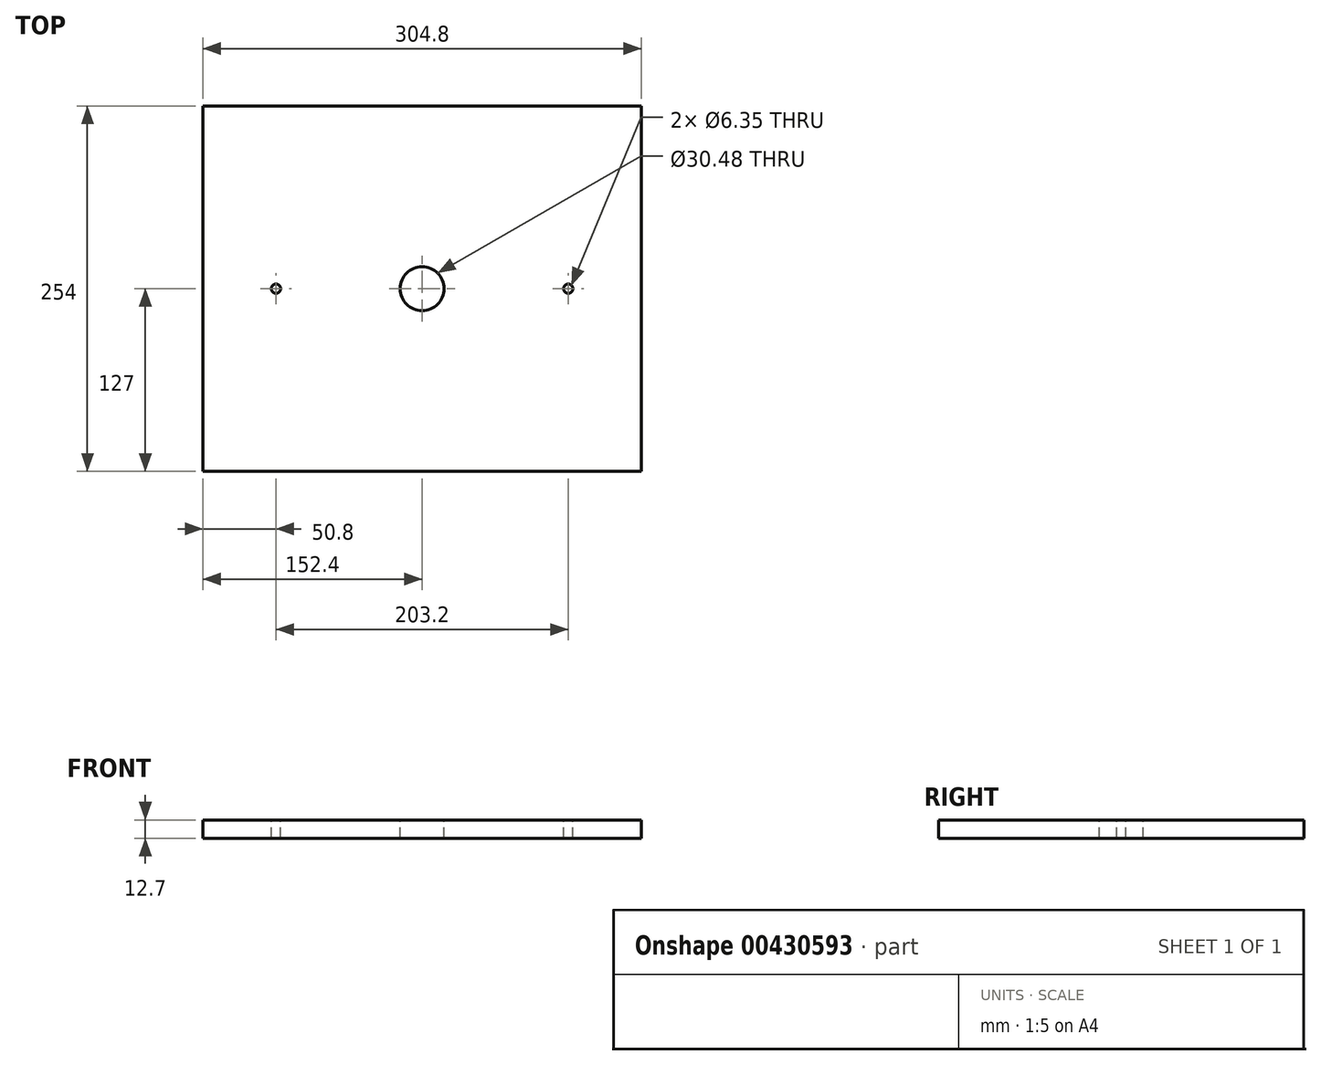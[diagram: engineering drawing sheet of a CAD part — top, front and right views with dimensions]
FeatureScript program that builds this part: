
annotation { "Feature Type Name" : "Feature", "Feature Type Description" : "" }
export const myFeature = defineFeature(function(context is Context, id is Id, definition is map)
    precondition{}
    {
        {
            var Q0;
            Q0=qCreatedBy(makeId("Top.planeOp"),FACE);
            var sketch = newSketch(context, id + "F0", { "sketchPlane" : qUnion([Q0])});
            skLineSegment(sketch, "E0.bottom", {"start": v(152.4, -127) * mm, "end": v(-152.4, -127) * mm});
            skLineSegment(sketch, "E0.top", {"start": v(152.4, 127) * mm, "end": v(-152.4, 127) * mm});
            skLineSegment(sketch, "E0.left", {"start": v(152.4, -127) * mm, "end": v(152.4, 127) * mm});
            skLineSegment(sketch, "E0.right", {"start": v(-152.4, -127) * mm, "end": v(-152.4, 127) * mm});
            skPoint(sketch, "E0.middle", {"position": v(0, 0) * mm});
            skSolve(sketch);
        }
        {
            var Q0;
            Q0=makeQuery(id+"F0.imprint","IMPRINT",FACE,{"disambiguationData":[TD([[makeQuery(id+"F0.imprint","IMPRINT",EDGE,{"derivedFrom":sQuery(id+"F0.wireOp",EDGE,"E0.bottom")}),-1.0]])]});
            extrude(context, id + "F1", {"entities" : qUnion([Q0]), "endBound" : BoundingType.SYMMETRIC, "depth" : 12.7 * mm});
        }
        {
            var Q0;
            Q0=makeQuery(id+"F1.opExtrude","CAP_FACE",FACE,{"disambiguationData":[OSD([sQuery(id+"F0.wireOp",EDGE,"E0.bottom"),sQuery(id+"F0.wireOp",EDGE,"E0.top"),sQuery(id+"F0.wireOp",EDGE,"E0.left"),sQuery(id+"F0.wireOp",EDGE,"E0.right")])],"isStart":false});
            var sketch = newSketch(context, id + "F2", { "sketchPlane" : qUnion([Q0])});
            skCircle(sketch, "E1", {"center": v(0, 0) * mm, "radius": 15.24 * mm});
            skSolve(sketch);
        }
        {
            var Q0;
            Q0=makeQuery(id+"F2.imprint","IMPRINT",FACE,{"disambiguationData":[TD([[makeQuery(id+"F2.imprint","IMPRINT",EDGE,{"derivedFrom":sQuery(id+"F2.wireOp",EDGE,"E1")}),1.0]])]});
            extrude(context, id + "F3", {"entities" : qUnion([Q0]), "operationType" : NewBodyOperationType.REMOVE, "endBound" : BoundingType.THROUGH_ALL, "oppositeDirection" : true, "depth" : 25.4 * mm});
        }
        {
            var Q0;
            Q0=makeQuery(id+"F1.opExtrude","CAP_FACE",FACE,{"disambiguationData":[OSD([sQuery(id+"F0.wireOp",EDGE,"E0.bottom"),sQuery(id+"F0.wireOp",EDGE,"E0.top"),sQuery(id+"F0.wireOp",EDGE,"E0.left"),sQuery(id+"F0.wireOp",EDGE,"E0.right")])],"isStart":false});
            var sketch = newSketch(context, id + "F4", { "sketchPlane" : qUnion([Q0])});
            skCircle(sketch, "E2", {"center": v(-101.6, 0) * mm, "radius": 3.18 * mm});
            skCircle(sketch, "E3", {"center": v(101.6, 0) * mm, "radius": 3.18 * mm});
            skSolve(sketch);
        }
        {
            var Q0;
            Q0 = qSketchRegion(id + "F4", true);
            extrude(context, id + "F5", {"entities" : qUnion([Q0]), "operationType" : NewBodyOperationType.REMOVE, "endBound" : BoundingType.THROUGH_ALL, "oppositeDirection" : true, "depth" : 25.4 * mm});
        }
    });
